# Revit family: 1286xxx Ascoli Twin CE
name_source: partatom
category: Lighting Fixtures
revit_build: Autodesk Revit 2018 (Build: 20170223_1515(x64)
units: mm (PartAtom-declared; Revit-internal decimal feet)

## family parameters
Always vertical = Yes
Cut with Voids When Loaded = No
Host = Ceiling
Light Source = No
OmniClass Number = 23.80.70.11
OmniClass Title = Luminaries for Internal Lighting
Part Type = Normal
Room Calculation Point = No
Round Connector Dimension = Use Diameter
Shared = No

## types (4) — shared parameters
Dimmable = Lamp Dependant
Dimming Method = Lamp Dependant
Driver Required = No
Efficacy (lm/w) = Lamp Dependant
Electrical Class = CE CLass II
IP Rating / Zone = IP20 / Zone 3
Lamp = GU10 LED
Main Material = Aluminium
Power (Watts) = 6W Max
Product CCT = Lamp Dependant
Product CRI = Lamp Dependant
Product Dimensions = 350 x 60 x 135 mm
Product Location = Ceiling / Wall - Installed out of reach
Product Name = Ascoli Twin
Product URL = https://www.astrolighting.com
Product Weight = 0.75 kg

## per-type parameters (varying)
| type | Main Finish | Product SKU |
| Ascoli Twin Bronze | Bronze | 1286035 |
| Ascoli Twin Textured White | Textured White | 1286034 |
| Ascoli Twin Matt Nickel | Matt Nickel | 1286036 |
| Ascoli Twin Matt Black | Matt Black | 1286081 |

## geometry (parser evidence)
native form markers: Sweep x2
no freeform markers — native parametric forms only
